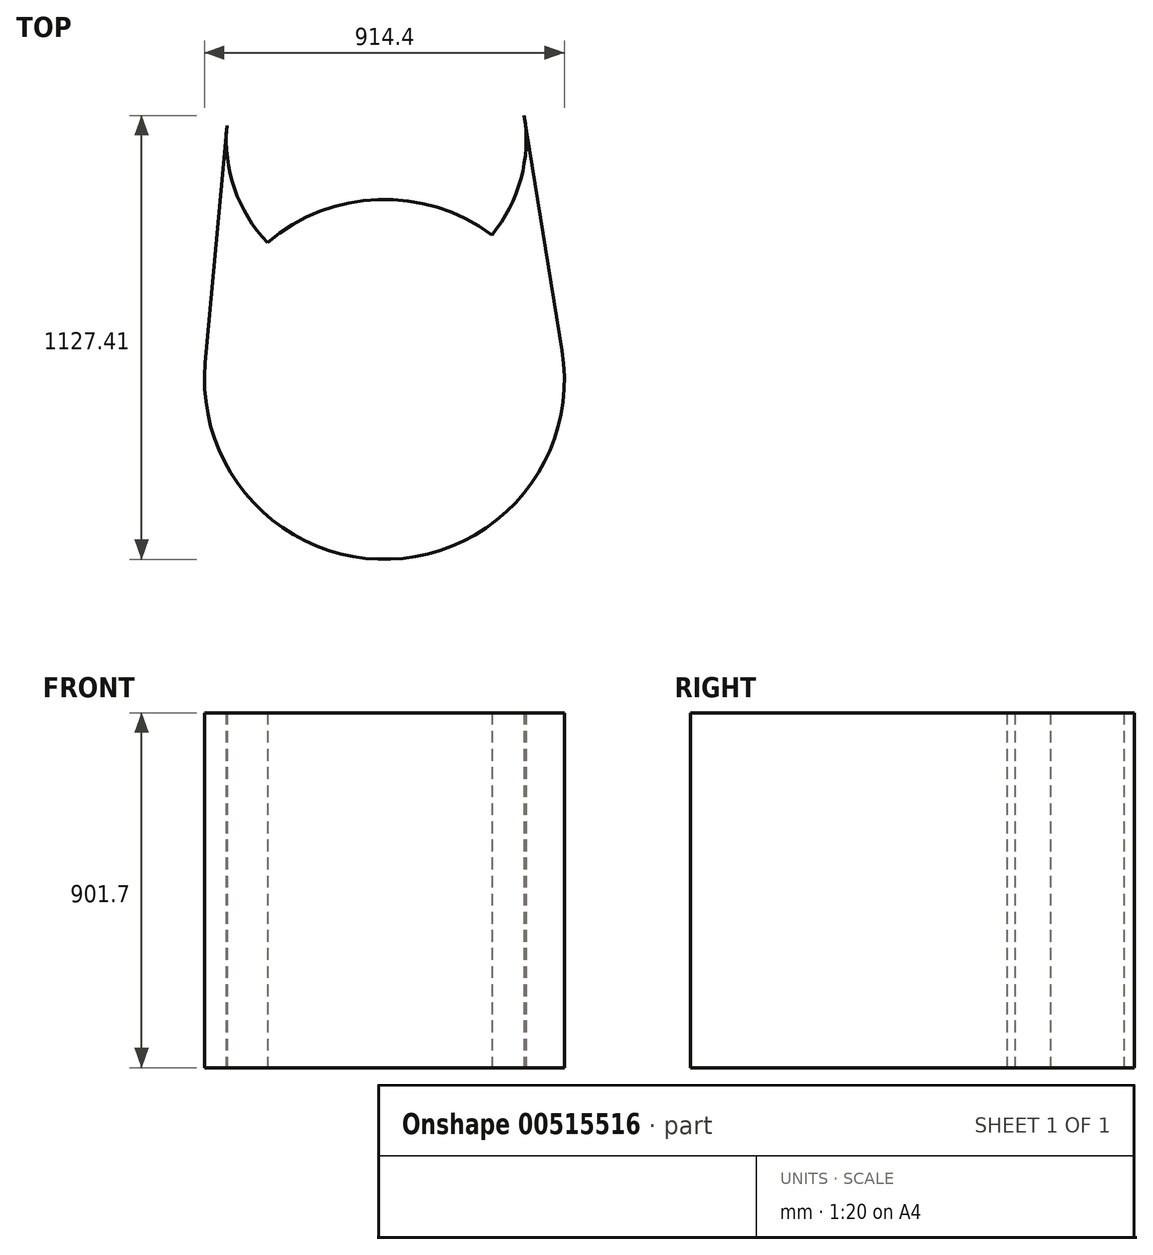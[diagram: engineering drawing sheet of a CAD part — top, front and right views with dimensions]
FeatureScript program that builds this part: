
annotation { "Feature Type Name" : "Feature", "Feature Type Description" : "" }
export const myFeature = defineFeature(function(context is Context, id is Id, definition is map)
    precondition{}
    {
        {
            var Q0;
            Q0=qCreatedBy(makeId("Top.planeOp"),FACE);
            var sketch = newSketch(context, id + "F0", { "sketchPlane" : qUnion([Q0])});
            skCircle(sketch, "E0", {"center": v(-21.05, -843.4) * mm, "radius": 381 * mm});
            skCircle(sketch, "E1", {"center": v(0, -1453) * mm, "radius": 457.2 * mm});
            skLineSegment(sketch, "E2", {"start": v(355.1, -782.8) * mm, "end": v(451.38, -1380.27) * mm});
            skLineSegment(sketch, "E3", {"start": v(-400.48, -808.88) * mm, "end": v(-455.32, -1411.57) * mm});
            skSolve(sketch);
        }
        {
            var Q0;
            {var subQ0=sQuery(id+"F0.wireOp",EDGE,"E3");Q0=makeQuery(id+"F0.imprint","IMPRINT",FACE,{"disambiguationData":[TD([[makeQuery(id+"F0.imprint","IMPRINT",EDGE,{"derivedFrom":subQ0}),1.0]])]});}
            var Q1;
            {var subQ0=sQuery(id+"F0.wireOp",EDGE,"E1");var subQ1=sQuery(id+"F0.wireOp",EDGE,"E0");var subQ2=makeQuery(id+"F0.imprint","INTERSECT",VERTEX,{"disambiguationData":[OD(0.0)],"derivedFrom":[subQ1,subQ0]});Q1=makeQuery(id+"F0.imprint","IMPRINT",FACE,{"disambiguationData":[TD([[makeQuery(id+"F0.imprint","IMPRINT",EDGE,{"disambiguationData":[TD([[subQ2,-1.0]])],"derivedFrom":subQ1}),1.0]])]});}
            var Q2;
            {var subQ0=sQuery(id+"F0.wireOp",EDGE,"E2");Q2=makeQuery(id+"F0.imprint","IMPRINT",FACE,{"disambiguationData":[TD([[makeQuery(id+"F0.imprint","IMPRINT",EDGE,{"derivedFrom":subQ0}),-1.0]])]});}
            var Q3;
            {var subQ0=sQuery(id+"F0.wireOp",EDGE,"E1");var subQ1=sQuery(id+"F0.wireOp",EDGE,"E0");var subQ2=makeQuery(id+"F0.imprint","INTERSECT",VERTEX,{"disambiguationData":[OD(0.0)],"derivedFrom":[subQ1,subQ0]});Q3=makeQuery(id+"F0.imprint","IMPRINT",FACE,{"disambiguationData":[TD([[makeQuery(id+"F0.imprint","IMPRINT",EDGE,{"disambiguationData":[TD([[subQ2,-1.0]])],"derivedFrom":subQ1}),-1.0]])]});}
            var Q4;
            Q4 = qSketchRegion(id + "F2", true);
            extrude(context, id + "F1", {"entities" : qUnion([Q0, Q1, Q2, Q3, Q4]), "depth" : 901.7 * mm, "offsetDistance" : 25.4 * mm});
        }
    });
